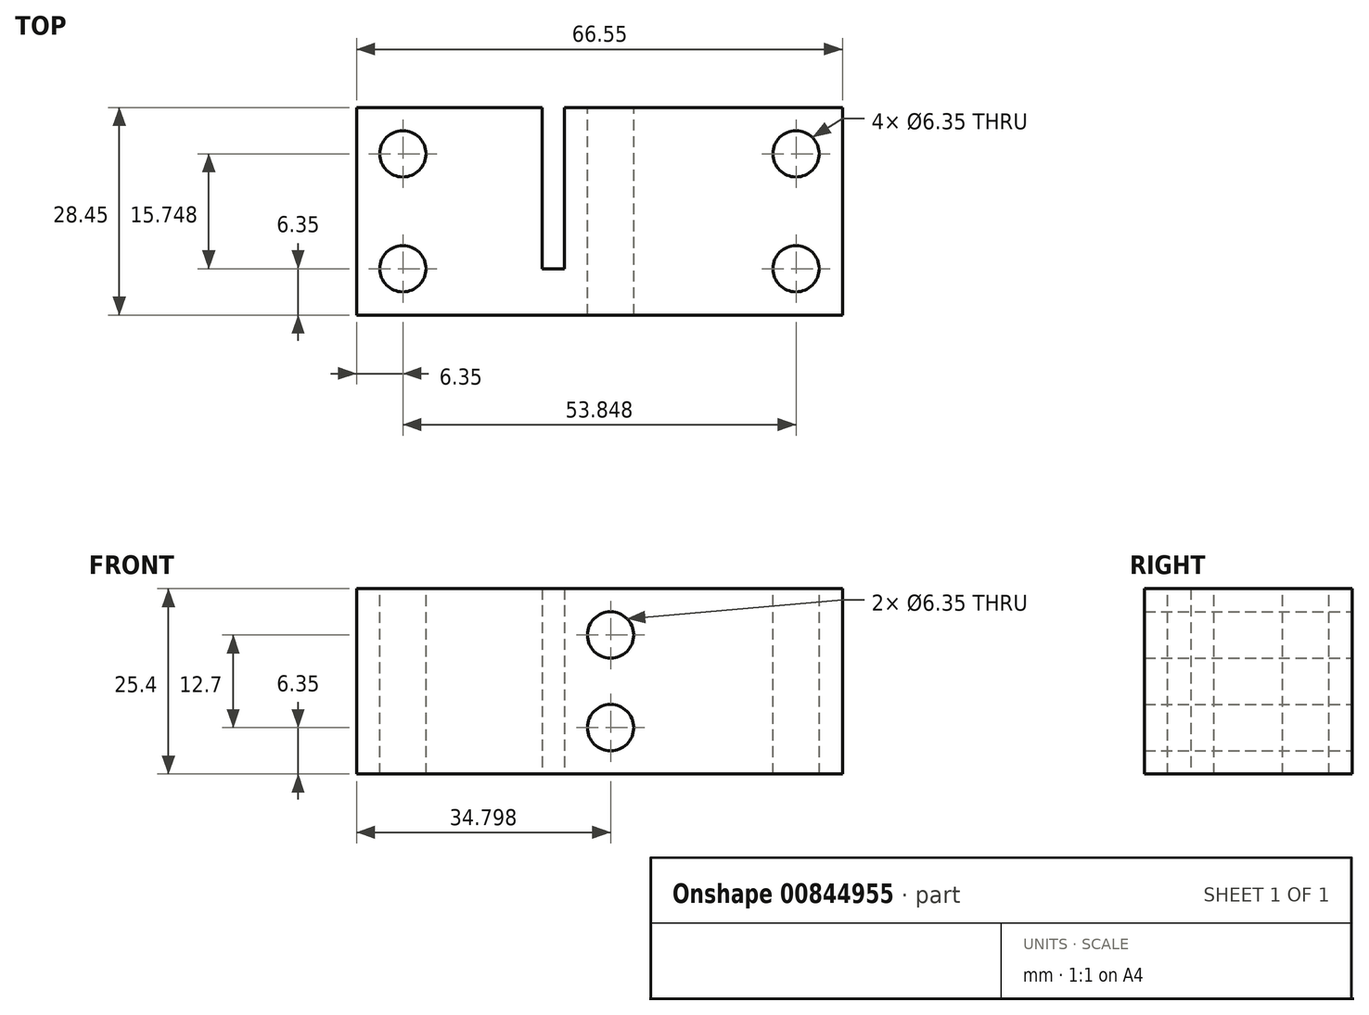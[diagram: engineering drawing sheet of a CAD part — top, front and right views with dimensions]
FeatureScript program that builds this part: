
annotation { "Feature Type Name" : "Feature", "Feature Type Description" : "" }
export const myFeature = defineFeature(function(context is Context, id is Id, definition is map)
    precondition{}
    {
        {
            var Q0;
            Q0=qCreatedBy(makeId("Top.planeOp"),FACE);
            var sketch = newSketch(context, id + "F0", { "sketchPlane" : qUnion([Q0])});
            skLineSegment(sketch, "E0", {"start": v(0, 0) * mm, "end": v(66.55, 0) * mm});
            skLineSegment(sketch, "E1", {"start": v(66.55, 0) * mm, "end": v(66.55, 28.45) * mm});
            skLineSegment(sketch, "E2", {"start": v(66.55, 28.45) * mm, "end": v(28.45, 28.45) * mm});
            skLineSegment(sketch, "E3", {"start": v(28.45, 28.45) * mm, "end": v(28.45, 6.35) * mm});
            skLineSegment(sketch, "E4", {"start": v(28.45, 6.35) * mm, "end": v(25.4, 6.35) * mm});
            skLineSegment(sketch, "E5", {"start": v(25.4, 6.35) * mm, "end": v(25.4, 28.45) * mm});
            skLineSegment(sketch, "E6", {"start": v(25.4, 28.45) * mm, "end": v(0, 28.45) * mm});
            skLineSegment(sketch, "E7", {"start": v(0, 28.45) * mm, "end": v(0, 0) * mm});
            skSolve(sketch);
        }
        {
            var Q0;
            Q0 = qSketchRegion(id + "F0", true);
            extrude(context, id + "F1", {"entities" : qUnion([Q0]), "depth" : 25.4 * mm, "offsetDistance" : 25.4 * mm});
        }
        {
            var Q0;
            Q0=makeQuery(id+"F1.opExtrude","CAP_FACE",FACE,{"disambiguationData":[OSD([sQuery(id+"F0.wireOp",EDGE,"E0"),sQuery(id+"F0.wireOp",EDGE,"E1"),sQuery(id+"F0.wireOp",EDGE,"E2"),sQuery(id+"F0.wireOp",EDGE,"E3"),sQuery(id+"F0.wireOp",EDGE,"E4"),sQuery(id+"F0.wireOp",EDGE,"E5"),sQuery(id+"F0.wireOp",EDGE,"E6"),sQuery(id+"F0.wireOp",EDGE,"E7")])],"isStart":false});
            var sketch = newSketch(context, id + "F2", { "sketchPlane" : qUnion([Q0])});
            skCircle(sketch, "E8", {"center": v(6.35, 6.35) * mm, "radius": 3.18 * mm});
            skCircle(sketch, "E9", {"center": v(60.2, 6.35) * mm, "radius": 3.18 * mm});
            skCircle(sketch, "E10", {"center": v(6.35, 22.1) * mm, "radius": 3.18 * mm});
            skCircle(sketch, "E11", {"center": v(60.2, 22.1) * mm, "radius": 3.18 * mm});
            skSolve(sketch);
        }
        {
            var Q0;
            Q0=makeQuery(id+"F2.imprint","IMPRINT",FACE,{"disambiguationData":[TD([[makeQuery(id+"F2.imprint","IMPRINT",EDGE,{"derivedFrom":sQuery(id+"F2.wireOp",EDGE,"E8")}),1.0]])]});
            var Q1;
            Q1=makeQuery(id+"F2.imprint","IMPRINT",FACE,{"disambiguationData":[TD([[makeQuery(id+"F2.imprint","IMPRINT",EDGE,{"derivedFrom":sQuery(id+"F2.wireOp",EDGE,"E9")}),1.0]])]});
            var Q2;
            Q2=makeQuery(id+"F2.imprint","IMPRINT",FACE,{"disambiguationData":[TD([[makeQuery(id+"F2.imprint","IMPRINT",EDGE,{"derivedFrom":sQuery(id+"F2.wireOp",EDGE,"E11")}),1.0]])]});
            var Q3;
            Q3=makeQuery(id+"F2.imprint","IMPRINT",FACE,{"disambiguationData":[TD([[makeQuery(id+"F2.imprint","IMPRINT",EDGE,{"derivedFrom":sQuery(id+"F2.wireOp",EDGE,"E10")}),1.0]])]});
            extrude(context, id + "F3", {"entities" : qUnion([Q0, Q1, Q2, Q3]), "operationType" : NewBodyOperationType.REMOVE, "oppositeDirection" : true, "depth" : 25.4 * mm, "offsetDistance" : 25.4 * mm});
        }
        {
            var Q0;
            Q0=makeQuery(id+"F1.opExtrude","SWEPT_FACE",FACE,{"disambiguationData":[OSD([sQuery(id+"F0.wireOp",EDGE,"E2")])]});
            var sketch = newSketch(context, id + "F4", { "sketchPlane" : qUnion([Q0])});
            skCircle(sketch, "E12", {"center": v(-34.8, 6.35) * mm, "radius": 3.18 * mm});
            skCircle(sketch, "E13", {"center": v(-34.8, 19.05) * mm, "radius": 3.18 * mm});
            skSolve(sketch);
        }
        {
            var Q0;
            Q0 = qSketchRegion(id + "F4", true);
            var Q1;
            Q1=makeQuery(id+"F1.opExtrude","SWEPT_FACE",FACE,{"disambiguationData":[OSD([sQuery(id+"F0.wireOp",EDGE,"E0")])]});
            extrude(context, id + "F5", {"entities" : qUnion([Q0]), "operationType" : NewBodyOperationType.REMOVE, "endBound" : BoundingType.UP_TO_SURFACE, "oppositeDirection" : true, "depth" : 25.4 * mm, "endBoundEntityFace" : qUnion([Q1]), "offsetDistance" : 25.4 * mm});
        }
    });
